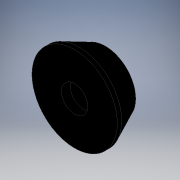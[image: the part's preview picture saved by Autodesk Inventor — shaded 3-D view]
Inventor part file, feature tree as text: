
AUTODESK INVENTOR PART (.ipt)
format: ipt  version: 2017.3 (Build 213256000, 256)  size: 114,176 bytes
history: native  units: mm
features: revolve x1, sketch x1
ambient origin geometry x8: Origin, YZ Plane, XZ Plane, XY Plane, X Axis, Y Axis, Z Axis, Center Point
bodies: Solid1 (feature_tree)
feature tree (2):
  revolve  "Revolution1"  [1 undecoded]
  sketch  "Sketch1"  dims[d0=2.875mm d1=1.5mm d2=1.0mm d3=3.45mm d4=3.5mm d5=4.85mm d6=0.5mm d7=90.0deg]
note: 1 required parameter value undecoded (feature->parameter linkage not recoverable at this tier; creation-order binding heuristic only, values carry confidence <= 0.55)
